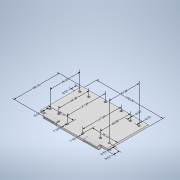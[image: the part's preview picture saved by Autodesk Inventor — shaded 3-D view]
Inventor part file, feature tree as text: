
AUTODESK INVENTOR PART (.ipt)
format: ipt  version: 2020 (Build 240168000, 168)  size: 300,544 bytes
history: native  units: mm
features: other x25, sketch x18, hole x12, extrude x6
ambient origin geometry x8: Origin, YZ Plane, XZ Plane, XY Plane, X Axis, Y Axis, Z Axis, Center Point
bodies: Solid1 (feature_tree)
feature tree (61):
  other  "Annotations"
  extrude  "Extrusion1"  Depth=62.1mm
  extrude  "Extrusion2"  Depth=42.1mm TaperAngle=0.0deg
  extrude  "Extrusion3"  Depth=6.0mm
  extrude  "Extrusion4"  Depth=57.89mm
  extrude  "Extrusion5"  Depth=6.0mm
  extrude  "Extrusion6"  Depth=8.95mm TaperAngle=0.0deg
  hole  "Hole1"  [1 undecoded]
  hole  "Hole2"  [1 undecoded]
  hole  "Hole3"  [1 undecoded]
  hole  "Hole4"  [1 undecoded]
  hole  "Hole5"  [1 undecoded]
  hole  "Hole6"  [1 undecoded]
  hole  "Hole7"  [1 undecoded]
  hole  "Hole8"  [1 undecoded]
  hole  "Hole10"  [1 undecoded]
  hole  "Hole9"  [1 undecoded]
  hole  "Hole12"  [1 undecoded]
  hole  "Hole11"  [1 undecoded]
  sketch  "Sketch1"  dims[d0=2.9mm d1=62.1mm]
  sketch  "Sketch3"  dims[d4=20.0mm d5=0.0mm d6=42.1mm d7=0.0mm]
  sketch  "Sketch4"  dims[d8=20.0mm d9=0.0mm]
  sketch  "Sketch5"  dims[d10=2.921mm d11=6.0mm d12=4.0mm d13=2.0mm d14=90.0deg d15=8.0mm d16=20.594885mm]
  sketch  "Sketch6"  dims[d17=2.921mm d18=6.0mm d19=4.0mm d20=2.0mm d21=90.0deg d22=8.0mm d23=20.594885mm]
  sketch  "Sketch7"  dims[d24=2.921mm d25=6.0mm d26=4.0mm d27=2.0mm d28=90.0deg d29=8.0mm d30=20.594885mm]
  sketch  "Sketch8"  dims[d31=2.921mm d32=6.0mm d33=4.0mm d34=2.0mm d35=90.0deg d36=8.0mm d37=20.594885mm d42=23.8mm]
  sketch  "Sketch9"  dims[d48=23.8mm d49=57.89mm]
  sketch  "Sketch10"  dims[d50=6.0mm d51=0.0mm d53=7.5mm]
  sketch  "Sketch11"  dims[d54=57.89mm d61=8.95mm d62=0.0mm]
  sketch  "Sketch12"  dims[d63=8.95mm d64=0.0mm]
  sketch  "Sketch13"  dims[d65=2.921mm d66=6.0mm d67=4.0mm d68=2.0mm d69=90.0deg d70=8.0mm d71=20.594885mm d80=38.1mm]
  sketch  "Sketch14"  dims[d81=7.5mm d82=38.1mm]
  sketch  "Sketch15"  dims[d84=2.921mm d85=6.0mm d86=4.0mm d87=2.0mm d88=90.0deg d89=8.0mm d90=20.594885mm]
  sketch  "Sketch16"  dims[d91=2.921mm d92=6.0mm d93=4.0mm d94=2.0mm d95=90.0deg d96=8.0mm d97=20.594885mm]
  sketch  "Sketch17"  dims[d98=2.921mm d99=6.0mm d100=4.0mm d101=2.0mm d102=90.0deg d103=8.0mm d104=20.594885mm]
  sketch  "Sketch18"  dims[d105=2.921mm d106=6.0mm d107=4.0mm d108=2.0mm d109=90.0deg d110=8.0mm d111=20.594885mm]
  sketch  "Sketch19"  dims[d112=2.921mm d113=6.0mm d114=4.0mm d115=2.0mm d116=90.0deg d117=8.0mm d118=20.594885mm d119=2.921mm d120=6.0mm d121=4.0mm d122=2.0mm d123=90.0deg d124=8.0mm d125=20.594885mm d126=2.921mm d127=6.0mm d128=4.0mm d129=2.0mm d130=90.0deg d131=8.0mm d132=20.594885mm d133=8.57mm d134=5.41mm d135=8.57mm d136=13.26mm d137=5.41mm d138=44.96mm d139=44.96mm d140=44.96mm d141=44.96mm d142=5.41mm d143=5.41mm d144=13.26mm d145=13.26mm d146=8.57mm d147=8.57mm d148=13.26mm d156=1.1mm d157=1.1mm d158=2.2mm d159=1.1mm d160=2.2mm d149=23.8mm d150=13.26mm d151=44.96mm d152=0.546068mm d153=8.57mm d154=5.128261mm d155=8.57mm d161=57.89mm d162=0.558582mm d163=38.1mm d164=9.6254mm d165=38.1mm d166=7.609769mm d167=7.5mm d168=1.989377mm d169=7.5mm d170=57.89mm d171=4.49951mm d172=8.57mm d173=8.054755mm d174=8.57mm d175=9.319579mm d176=8.57mm d177=7.354142mm d178=8.57mm d179=44.96mm d180=44.96mm d181=44.96mm d182=44.96mm d58=8.720877mm d59=0.837125mm d60=68.1mm d72=1.978463mm d73=6.235219mm d74=100.0mm d75=6.886257mm d76=38.1mm d77=1.822575mm d78=38.1mm d83=57.89mm]
  other  "Linear Dimension 5"
  other  "Linear Dimension 6"
  other  "Linear Dimension 7"
  other  "Linear Dimension 8"
  other  "Linear Dimension 9"
  other  "Linear Dimension 10"
  other  "Linear Dimension 11"
  other  "Linear Dimension 12"
  other  "Linear Dimension 13"
  other  "Linear Dimension 14"
  other  "Linear Dimension 15"
  other  "Linear Dimension 16"
  other  "Linear Dimension 17"
  other  "Linear Dimension 18"
  other  "Linear Dimension 19"
  other  "Linear Dimension 20"
  other  "Linear Dimension 21"
  other  "Linear Dimension 22"
  other  "Linear Dimension 23"
  other  "Linear Dimension 24"
  other  "Linear Dimension 25"
  other  "Linear Dimension 26"
  other  "Linear Dimension 27"
  other  "Linear Dimension 28"
note: 12 required parameter values undecoded (feature->parameter linkage not recoverable at this tier; creation-order binding heuristic only, values carry confidence <= 0.55)
